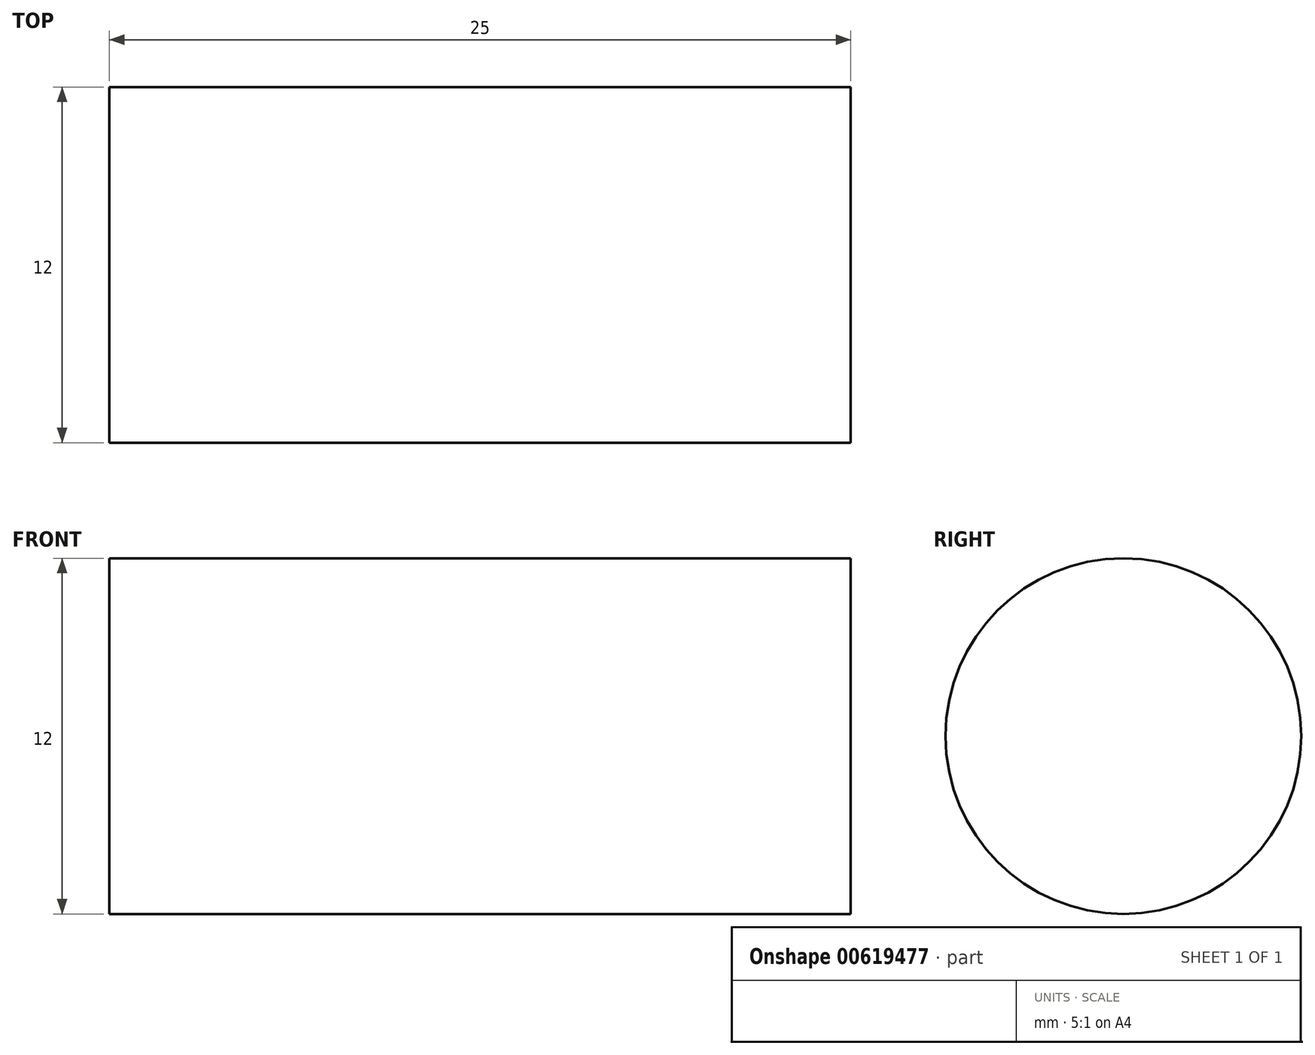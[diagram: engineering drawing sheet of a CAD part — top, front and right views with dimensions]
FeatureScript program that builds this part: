
annotation { "Feature Type Name" : "Feature", "Feature Type Description" : "" }
export const myFeature = defineFeature(function(context is Context, id is Id, definition is map)
    precondition{}
    {
        {
            var Q0;
            Q0=qCreatedBy(makeId("Right.planeOp"),FACE);
            var sketch = newSketch(context, id + "F0", { "sketchPlane" : qUnion([Q0])});
            skCircle(sketch, "E0", {"center": v(0, 0) * mm, "radius": 6 * mm});
            skSolve(sketch);
        }
        {
            var Q0;
            Q0=makeQuery(id+"F0.imprint","IMPRINT",FACE,{"disambiguationData":[TD([[makeQuery(id+"F0.imprint","IMPRINT",EDGE,{"derivedFrom":sQuery(id+"F0.wireOp",EDGE,"E0")}),1.0]])]});
            extrude(context, id + "F1", {"entities" : qUnion([Q0]), "depth" : 25 * mm, "offsetDistance" : 25.4 * mm});
        }
    });
